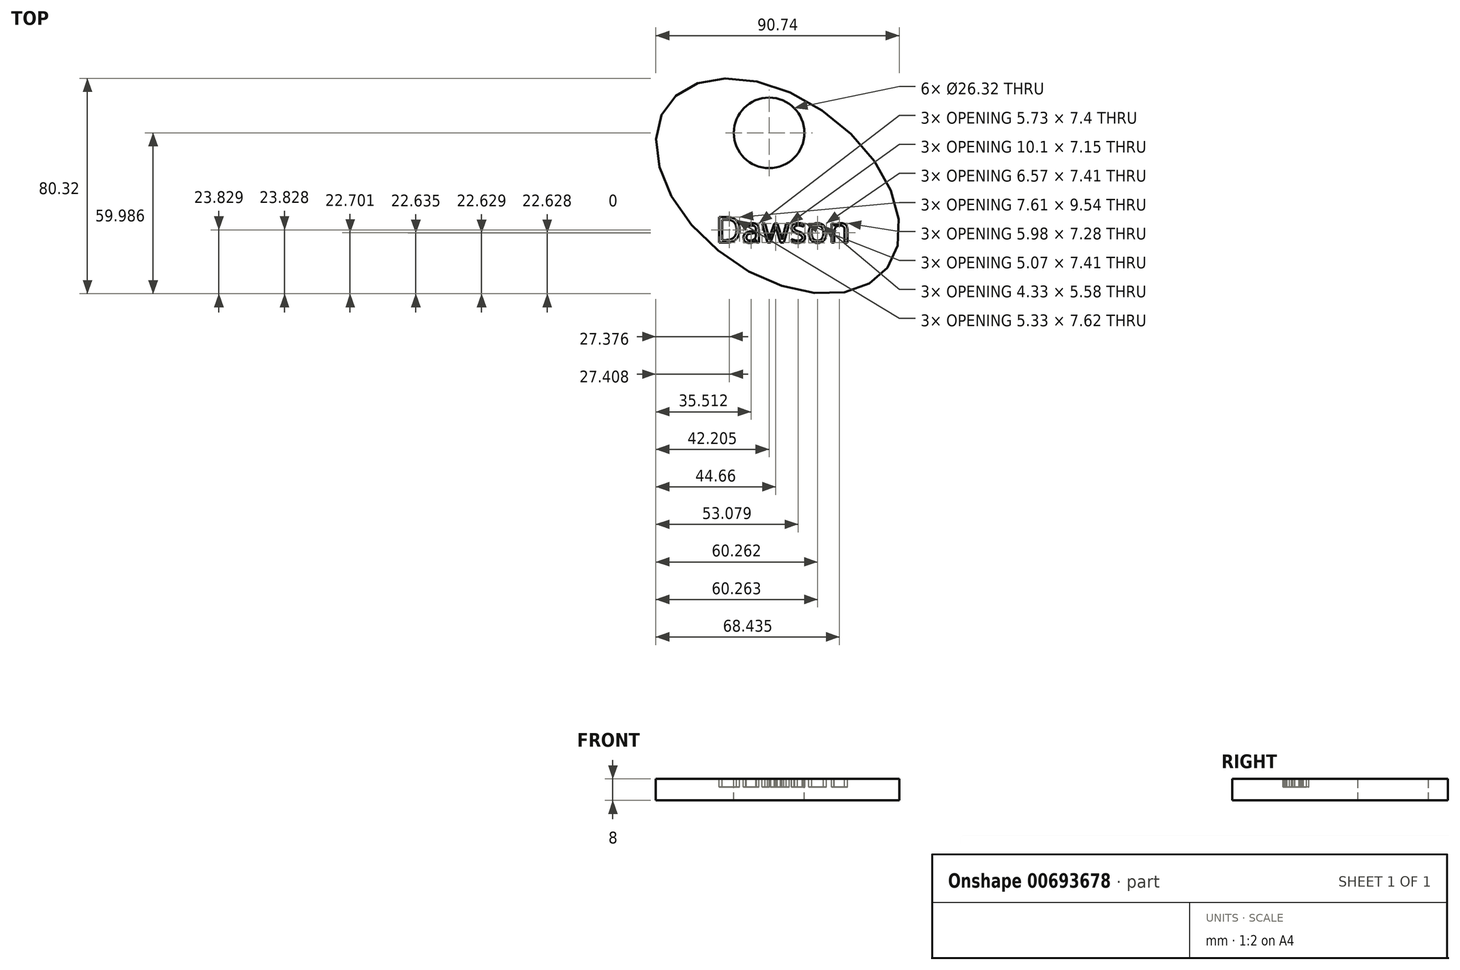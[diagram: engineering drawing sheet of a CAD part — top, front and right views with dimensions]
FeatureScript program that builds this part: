
annotation { "Feature Type Name" : "Feature", "Feature Type Description" : "" }
export const myFeature = defineFeature(function(context is Context, id is Id, definition is map)
    precondition{}
    {
        {
            var Q0;
            Q0=qCreatedBy(makeId("Top.planeOp"),FACE);
            var sketch = newSketch(context, id + "F0", { "sketchPlane" : qUnion([Q0])});
            skPoint(sketch, "E0.0.midPoint", {"position": v(-338.47, 83.2) * mm});
            skPoint(sketch, "E1.orphan", {"position": v(-194.36, 701.63) * mm});
            skPoint(sketch, "E0.cCircle.center.orphan", {"position": v(18.58, 0) * mm});
            skPoint(sketch, "E0.2.end.orphan", {"position": v(-482.59, -535.23) * mm});
            skEllipse(sketch, "E2", {"center": v(-26.92, 26.64) * mm, "majorRadius": 51.04 * mm, "minorRadius": 32.64 * mm, "majorAxis": v(0.8, -0.6)});
            skSolve(sketch);
        }
        {
            var Q0;
            Q0 = qSketchRegion(id + "F0", true);
            extrude(context, id + "F1", {"entities" : qUnion([Q0]), "depth" : 8 * mm, "offsetDistance" : 25 * mm});
        }
        {
            var Q0;
            Q0=makeQuery(id+"F1.opExtrude","CAP_FACE",FACE,{"disambiguationData":[OSD([sQuery(id+"F0.wireOp",EDGE,"E2")])],"isStart":false});
            var sketch = newSketch(context, id + "F2", { "sketchPlane" : qUnion([Q0])});
            skText(sketch, "E3", { "text": "Dawson\n", "fontName": "OpenSans-Regular.ttf"});
            const initialGuessF2  = {"E3": [-0.05, 0.00554, 1, 0, 0.00962]};
            skSetInitialGuess(sketch, initialGuessF2);
            skSolve(sketch);
        }
        {
            var Q0;
            Q0 = qSketchRegion(id + "F2", true);
            extrude(context, id + "F3", {"entities" : qUnion([Q0]), "operationType" : NewBodyOperationType.REMOVE, "oppositeDirection" : true, "depth" : 3 * mm, "offsetDistance" : 25 * mm});
        }
        {
            var Q0;
            {var subQ0=sQuery(id+"F0.wireOp",EDGE,"E2");Q0=makeQuery(id+"F3.boolean.opBoolean","SPLIT",FACE,{"disambiguationData":[TD([makeQuery(id+"F1.opExtrude","SWEPT_FACE",FACE,{"disambiguationData":[OSD([subQ0])]})])],"derivedFrom":makeQuery(id+"F1.opExtrude","CAP_FACE",FACE,{"disambiguationData":[OSD([subQ0])],"isStart":false})});}
            var sketch = newSketch(context, id + "F4", { "sketchPlane" : qUnion([Q0])});
            skCircle(sketch, "E4", {"center": v(-30.08, 46.47) * mm, "radius": 13.16 * mm});
            skSolve(sketch);
        }
        {
            var Q0;
            Q0=makeQuery(id+"F4.imprint","IMPRINT",FACE,{"disambiguationData":[TD([[makeQuery(id+"F4.imprint","IMPRINT",EDGE,{"derivedFrom":sQuery(id+"F4.wireOp",EDGE,"E4")}),1.0]])]});
            extrude(context, id + "F5", {"entities" : qUnion([Q0]), "operationType" : NewBodyOperationType.REMOVE, "oppositeDirection" : true, "depth" : 8 * mm, "offsetDistance" : 25 * mm});
        }
    });
